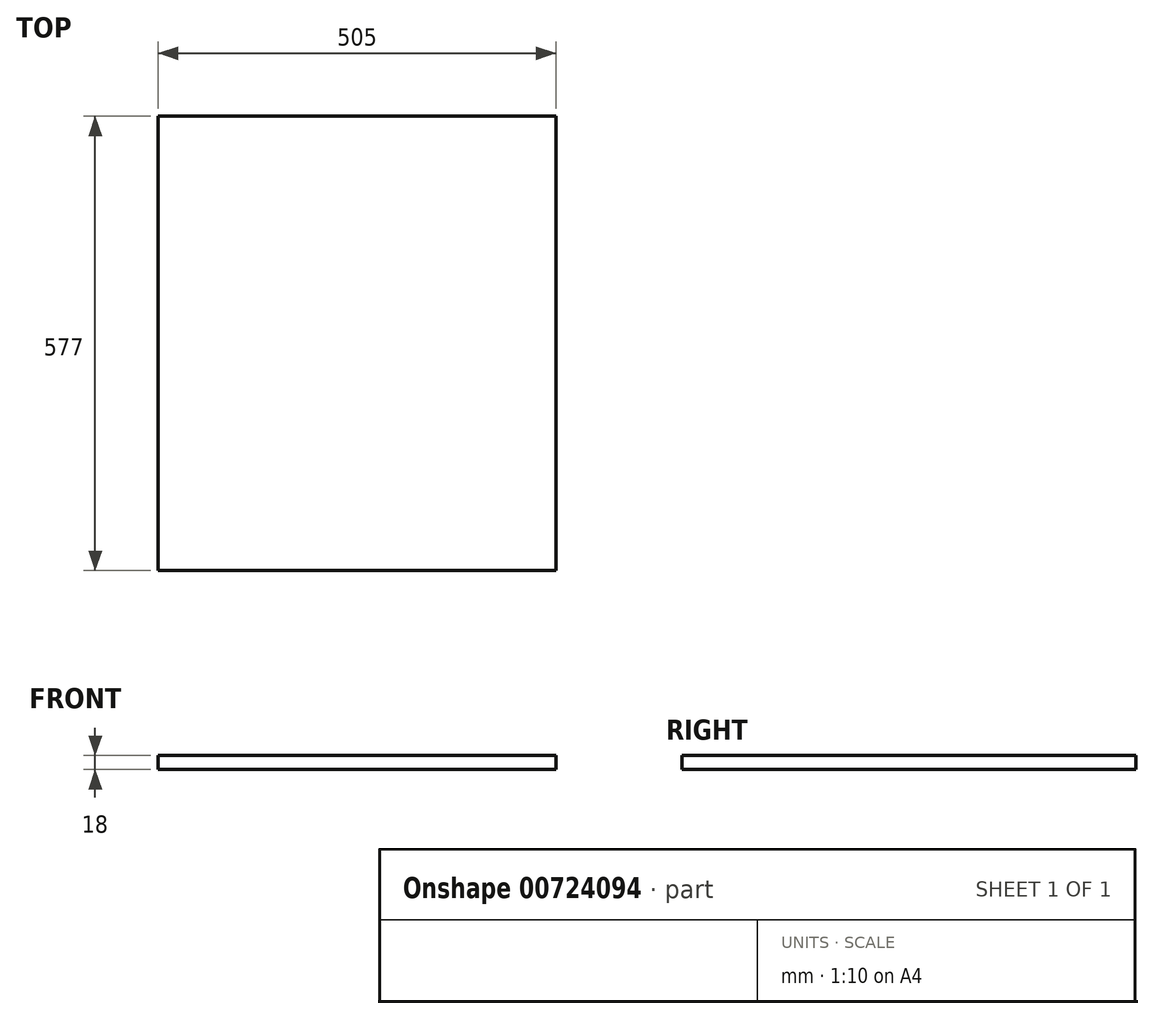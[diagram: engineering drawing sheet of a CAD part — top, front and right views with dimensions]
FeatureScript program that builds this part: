
annotation { "Feature Type Name" : "Feature", "Feature Type Description" : "" }
export const myFeature = defineFeature(function(context is Context, id is Id, definition is map)
    precondition{}
    {
        {
            var Q0;
            Q0=qCreatedBy(makeId("Top.planeOp"),FACE);
            var sketch = newSketch(context, id + "F0", { "sketchPlane" : qUnion([Q0])});
            skLineSegment(sketch, "E0.bottom", {"start": v(-252.5, 288.5) * mm, "end": v(252.5, 288.5) * mm});
            skLineSegment(sketch, "E0.top", {"start": v(-252.5, -288.5) * mm, "end": v(252.5, -288.5) * mm});
            skLineSegment(sketch, "E0.left", {"start": v(-252.5, 288.5) * mm, "end": v(-252.5, -288.5) * mm});
            skLineSegment(sketch, "E0.right", {"start": v(252.5, 288.5) * mm, "end": v(252.5, -288.5) * mm});
            skLineSegment(sketch, "E1", {"start": v(-252.5, 288.5) * mm, "end": v(252.5, -288.5) * mm, "construction": true});
            skSolve(sketch);
        }
        {
            var Q0;
            Q0 = qSketchRegion(id + "F0", true);
            extrude(context, id + "F1", {"entities" : qUnion([Q0]), "depth" : 18 * mm, "offsetDistance" : 25 * mm});
        }
    });
